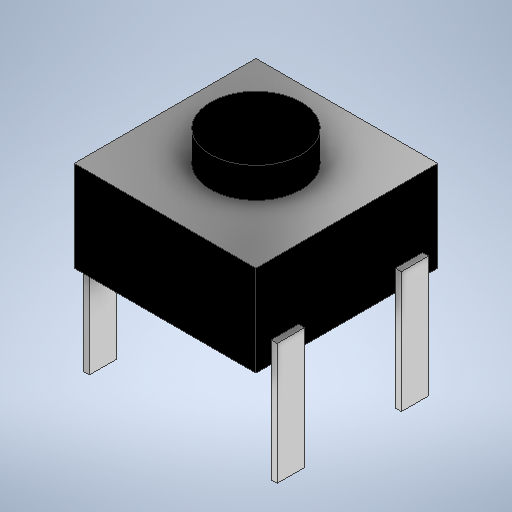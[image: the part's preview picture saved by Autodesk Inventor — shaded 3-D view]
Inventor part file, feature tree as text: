
AUTODESK INVENTOR PART (.ipt)
format: ipt  version: 2025.2 (Build 292293000, 293)  size: 285,696 bytes
history: native  units: mm
features: extrude x4, sketch x4
ambient origin geometry x8: Origin, YZ Plane, XZ Plane, XY Plane, X Axis, Y Axis, Z Axis, Center Point
bodies: Solid1 (feature_tree)
feature tree (8):
  extrude  "Extrusion1"  Depth=6.0mm
  extrude  "Extrusion2"  Depth=3.0mm
  extrude  "Extrusion3"  Depth=3.0mm
  extrude  "Extrusion4"  Depth=0.9mm
  sketch  "Sketch1"  dims[d0=6.0mm d1=6.0mm]
  sketch  "Sketch2"  dims[d2=3.0mm d3=0.0mm d4=3.0mm]
  sketch  "Sketch4"  dims[d5=3.0mm d6=3.0mm]
  sketch  "Sketch5"  dims[d7=1.0mm d8=0.0mm d9=0.9mm d10=0.7mm d11=3.3mm d12=0.5mm d13=0.0mm d14=0.2mm d15=0.0mm d16=0.2mm d17=0.0mm]
